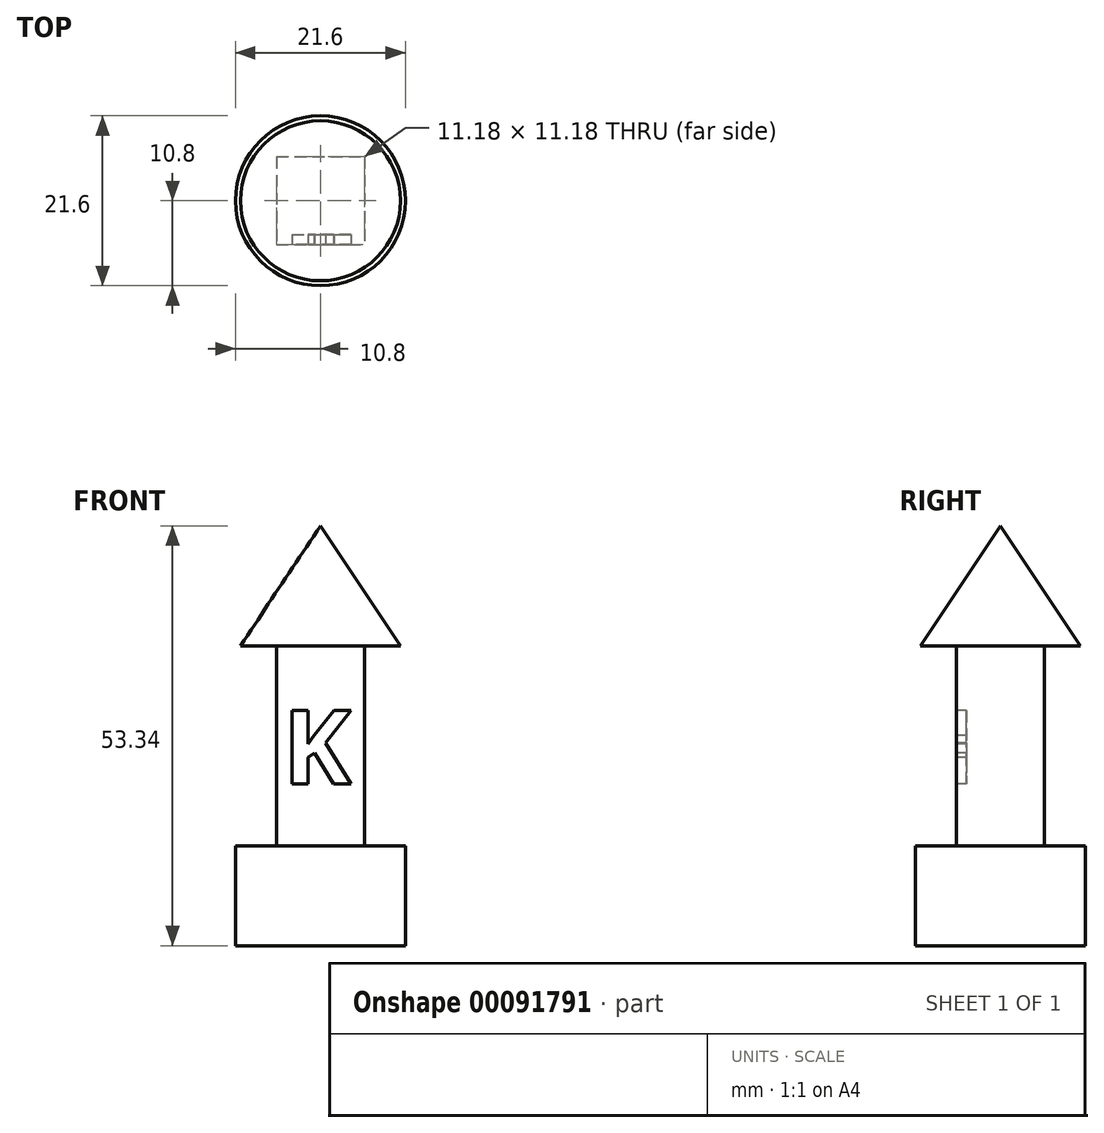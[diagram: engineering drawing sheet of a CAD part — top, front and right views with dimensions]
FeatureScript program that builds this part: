
annotation { "Feature Type Name" : "Feature", "Feature Type Description" : "" }
export const myFeature = defineFeature(function(context is Context, id is Id, definition is map)
    precondition{}
    {
        {
            var Q0;
            Q0=qCreatedBy(makeId("Top.planeOp"),FACE);
            var sketch = newSketch(context, id + "F0", { "sketchPlane" : qUnion([Q0])});
            skCircle(sketch, "E0", {"center": v(0, 0) * mm, "radius": 10.8 * mm});
            skSolve(sketch);
        }
        {
            var Q0;
            Q0 = qSketchRegion(id + "F0", true);
            extrude(context, id + "F1", {"entities" : qUnion([Q0]), "depth" : 12.7 * mm});
        }
        {
            var Q0;
            Q0=qCreatedBy(makeId("Top.planeOp"),FACE);
            var sketch = newSketch(context, id + "F2", { "sketchPlane" : qUnion([Q0])});
            skLineSegment(sketch, "E1.bottom", {"start": v(5.59, -5.59) * mm, "end": v(-5.59, -5.59) * mm});
            skLineSegment(sketch, "E1.top", {"start": v(5.59, 5.59) * mm, "end": v(-5.59, 5.59) * mm});
            skLineSegment(sketch, "E1.left", {"start": v(5.59, -5.59) * mm, "end": v(5.59, 5.59) * mm});
            skLineSegment(sketch, "E1.right", {"start": v(-5.59, -5.59) * mm, "end": v(-5.59, 5.59) * mm});
            skPoint(sketch, "E1.middle", {"position": v(0, 0) * mm});
            skSolve(sketch);
        }
        {
            var Q0;
            Q0 = qSketchRegion(id + "F2", true);
            extrude(context, id + "F3", {"entities" : qUnion([Q0]), "operationType" : NewBodyOperationType.ADD, "depth" : 38.1 * mm});
        }
        {
            var Q0;
            Q0=qCreatedBy(makeId("Right.planeOp"),FACE);
            var sketch = newSketch(context, id + "F4", { "sketchPlane" : qUnion([Q0])});
            skLineSegment(sketch, "E2", {"start": v(0, 0) * mm, "end": v(0, 38.1) * mm, "construction": true});
            skLineSegment(sketch, "E3", {"start": v(0, 38.1) * mm, "end": v(0, 53.34) * mm});
            skLineSegment(sketch, "E4", {"start": v(0, 53.34) * mm, "end": v(-10.16, 38.1) * mm});
            skLineSegment(sketch, "E5", {"start": v(0, 38.1) * mm, "end": v(-10.16, 38.1) * mm});
            skSolve(sketch);
        }
        {
            var Q0;
            Q0 = qSketchRegion(id + "F4", true);
            var Q1;
            Q1=sQuery(id+"F4.wireOp",EDGE,"E3");
            revolve(context, id + "F5", {"operationType" : NewBodyOperationType.ADD, "entities" : qUnion([Q0]), "axis" : qUnion([Q1]), "revolveType" : RevolveType.FULL});
        }
        {
            var Q0;
            Q0=makeQuery(id+"F3.opExtrude","SWEPT_FACE",FACE,{"disambiguationData":[OSD([sQuery(id+"F2.wireOp",EDGE,"E1.bottom")])]});
            var sketch = newSketch(context, id + "F6", { "sketchPlane" : qUnion([Q0])});
            skText(sketch, "E6", { "text": "K", "fontName": "OpenSans-Bold.ttf"});
            skLineSegment(sketch, "E7", {"start": v(0.02, 20.57) * mm, "end": v(0, 0.5) * mm, "construction": true});
            const initialGuessF6  = {"E6": [-0.00475, 0.02057, 1, 0, 0.0094]};
            skSetInitialGuess(sketch, initialGuessF6);
            skSolve(sketch);
        }
        {
            var Q0;
            Q0 = qSketchRegion(id + "F6", true);
            extrude(context, id + "F7", {"entities" : qUnion([Q0]), "operationType" : NewBodyOperationType.REMOVE, "oppositeDirection" : true, "depth" : 1.27 * mm});
        }
    });
